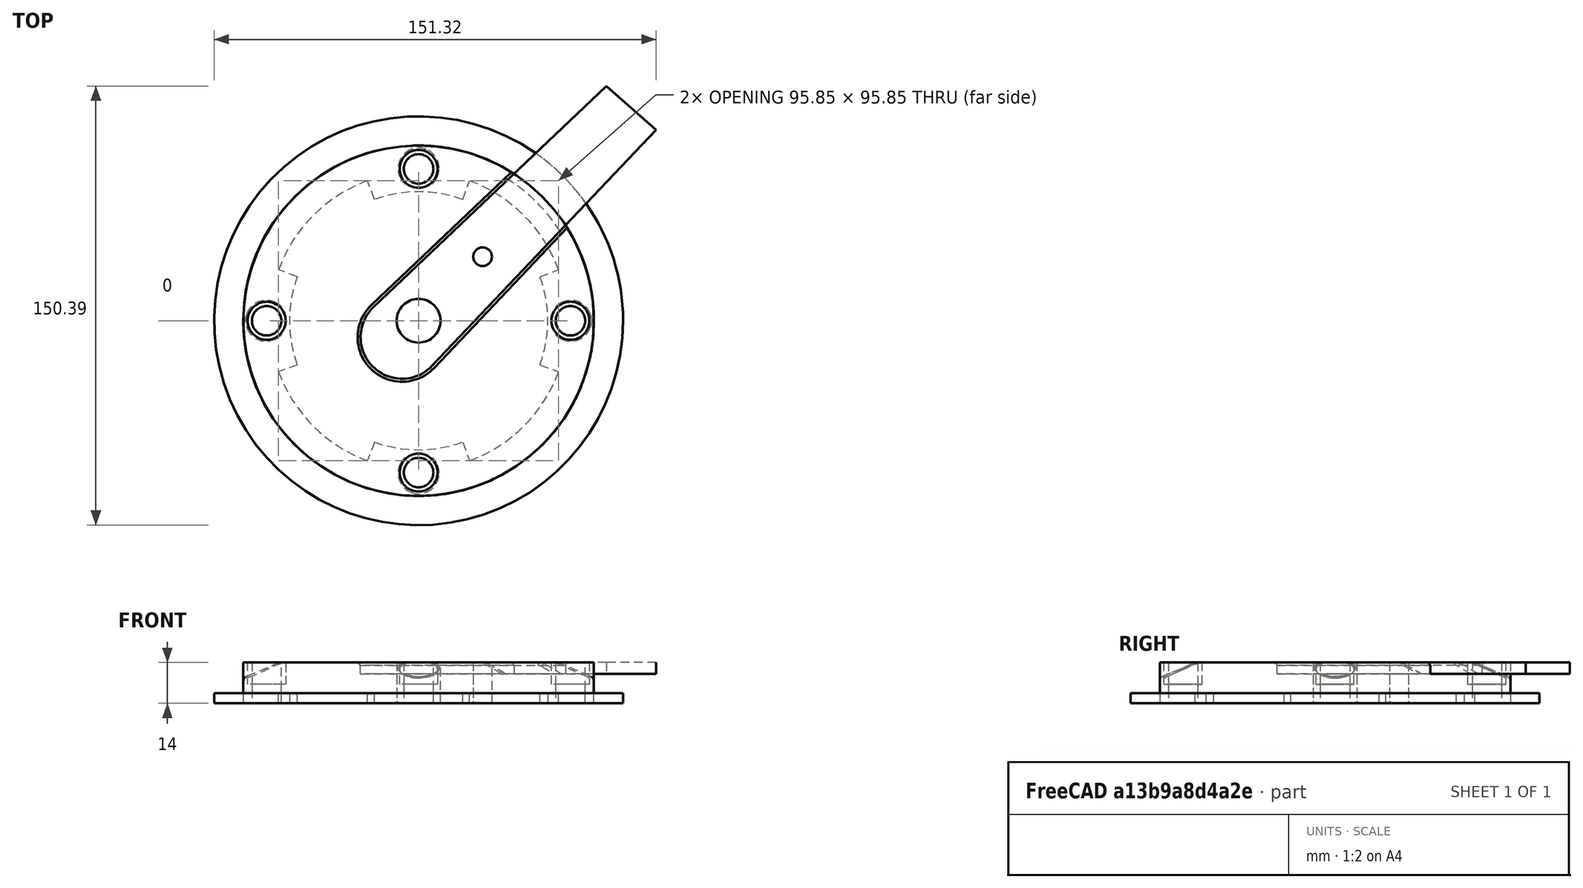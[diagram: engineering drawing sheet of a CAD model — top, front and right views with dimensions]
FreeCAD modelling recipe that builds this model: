
FCSTD DOCUMENT  (FreeCAD 0.16R)
Label: 104BCDspider_02
License: All rights reserved
LicenseURL: http://en.wikipedia.org/wiki/All_rights_reserved
objects: Sketcher::SketchObject×4, PartDesign::Fillet×4, PartDesign::Pocket×3, PartDesign::Pad×1, PartDesign::Chamfer×1, Part::Cone×1, Part::Common×1, Mesh::Feature×1
note: 19 computed .brp shape members not serialized (recipe doc carries the construction recipe); baked Part::Feature solids carry a one-line shape summary decoded from their .brp

FEATURE [Sketcher::SketchObject] Sketch
  sketch-geometry (9):
    g0: Circle [constr] CenterX=0 CenterY=0 CenterZ=0 NormalX=0 NormalY=0 NormalZ=1 Radius=52
    g1: Circle CenterX=0 CenterY=0 CenterZ=0 NormalX=0 NormalY=0 NormalZ=1 Radius=7.5
    g2: Circle CenterX=21.9203 CenterY=21.9203 CenterZ=0 NormalX=0 NormalY=0 NormalZ=1 Radius=3.2
    g3: Circle CenterX=0 CenterY=0 CenterZ=0 NormalX=0 NormalY=0 NormalZ=1 Radius=60
    g4: Circle CenterX=-52 CenterY=0 CenterZ=0 NormalX=0 NormalY=0 NormalZ=1 Radius=5.05
    g5: Circle CenterX=52 CenterY=0 CenterZ=0 NormalX=0 NormalY=0 NormalZ=1 Radius=5.05
    g6: Circle CenterX=0 CenterY=52 CenterZ=0 NormalX=0 NormalY=0 NormalZ=1 Radius=5.05
    g7: Circle CenterX=0 CenterY=-52 CenterZ=0 NormalX=0 NormalY=0 NormalZ=1 Radius=5.05
    g8: LineSegment [constr] StartX=0 StartY=0 StartZ=0 EndX=60.5216 EndY=60.5216 EndZ=0
  constraints (23):
    c: Coincident(g1,g-1)
    c: Coincident(g0,g-1)
    c: Radius(g0) = 52
    c: Radius(g1) = 7.5
    c: Radius(g2) = 3.2
    c: Coincident(g3,g-1)
    c: Radius(g3) = 60
    c: PointOnObject(g5,g-1)
    c: PointOnObject(g4,g-1)
    c: PointOnObject(g7,g-2)
    c: PointOnObject(g6,g-2)
    c: Radius(g7) = 5.05
    c: Equal(g7,g6)
    c: Equal(g7,g5)
    c: Equal(g7,g4)
    c: DistanceY(g7) = -52
    c: DistanceX(g5) = 52
    c: DistanceY(g6) = 52
    c: DistanceX(g4) = -52
    c: Distance(g-1,g2) = 31
    c: Coincident(g8,g-1)
    c: Angle(g8) = 0.785398
    c: PointOnObject(g2,g8)
FEATURE [PartDesign::Pad] Pad  label="Body14"
  Length = 14
  Length2 = 100
  Sketch = -> Sketch
  Type = 0
FEATURE [Sketcher::SketchObject] Sketch001
  Placement = pos=(0,0,0) rot=(1,0,0;3.14159rad)
  Support = -> Pad [Face8]
  sketch-geometry (17):
    g0: ArcOfCircle CenterX=0 CenterY=0 CenterZ=0 NormalX=0 NormalY=0 NormalZ=1 Radius=44.2 StartAngle=2.79253 EndAngle=3.49066
    g1: Circle CenterX=0 CenterY=0 CenterZ=0 NormalX=0 NormalY=0 NormalZ=1 Radius=70
    g2: ArcOfCircle CenterX=0 CenterY=0 CenterZ=0 NormalX=0 NormalY=0 NormalZ=1 Radius=51 StartAngle=1.91986 EndAngle=2.79253
    g3: LineSegment StartX=15.1173 StartY=41.5344 StartZ=0 EndX=17.443 EndY=47.9243 EndZ=0
    g4: LineSegment StartX=41.5344 StartY=15.1173 StartZ=0 EndX=47.9243 EndY=17.443 EndZ=0
    g5: LineSegment StartX=41.5344 StartY=-15.1173 StartZ=0 EndX=47.9243 EndY=-17.443 EndZ=0
    g6: LineSegment StartX=15.1173 StartY=-41.5344 StartZ=0 EndX=17.443 EndY=-47.9243 EndZ=0
    g7: LineSegment StartX=-15.1173 StartY=-41.5344 StartZ=0 EndX=-17.443 EndY=-47.9243 EndZ=0
    g8: LineSegment StartX=-41.5344 StartY=-15.1173 StartZ=0 EndX=-47.9243 EndY=-17.443 EndZ=0
    g9: LineSegment StartX=-41.5344 StartY=15.1173 StartZ=0 EndX=-47.9243 EndY=17.443 EndZ=0
    g10: LineSegment StartX=-15.1173 StartY=41.5344 StartZ=0 EndX=-17.443 EndY=47.9243 EndZ=0
    g11: ArcOfCircle CenterX=0 CenterY=0 CenterZ=0 NormalX=0 NormalY=0 NormalZ=1 Radius=51 StartAngle=0.349066 EndAngle=1.22173
    g12: ArcOfCircle CenterX=0 CenterY=0 CenterZ=0 NormalX=0 NormalY=0 NormalZ=1 Radius=51 StartAngle=5.06145 EndAngle=5.93412
    g13: ArcOfCircle CenterX=0 CenterY=0 CenterZ=0 NormalX=0 NormalY=0 NormalZ=1 Radius=51 StartAngle=3.49066 EndAngle=4.36332
    g14: ArcOfCircle CenterX=0 CenterY=0 CenterZ=0 NormalX=0 NormalY=0 NormalZ=1 Radius=44.2 StartAngle=1.22173 EndAngle=1.91986
    g15: ArcOfCircle CenterX=0 CenterY=0 CenterZ=0 NormalX=0 NormalY=0 NormalZ=1 Radius=44.2 StartAngle=5.93412 EndAngle=6.63225
    g16: ArcOfCircle CenterX=0 CenterY=0 CenterZ=0 NormalX=0 NormalY=0 NormalZ=1 Radius=44.2 StartAngle=4.36332 EndAngle=5.06145
  constraints (42):
    c: Coincident(g-1,g0)
    c: Radius(g0) = 44.2
    c: Coincident(g-1,g1)
    c: Radius(g1) = 70
    c: Coincident(g2,g-1)
    c: Radius(g2) = 51
    c: Angle(g3) = 1.22173
    c: Angle(g4) = 0.349066
    c: Angle(g5) = -0.349066
    c: Angle(g6) = -1.22173
    c: Angle(g7) = -1.91986
    c: Angle(g8) = -2.79253
    c: Angle(g9) = 2.79253
    c: Angle(g10) = 1.91986
    c: Equal(g2,g11)
    c: Coincident(g2,g11)
    c: Equal(g2,g12)
    c: Coincident(g2,g12)
    c: Equal(g2,g13)
    c: Coincident(g2,g13)
    c: Equal(g0,g14)
    c: Coincident(g0,g14)
    c: Equal(g0,g15)
    c: Coincident(g0,g15)
    c: Equal(g0,g16)
    c: Coincident(g0,g16)
    c: Coincident(g10,g14)
    c: Coincident(g3,g14)
    c: Coincident(g4,g15)
    c: Coincident(g5,g15)
    c: Coincident(g6,g16)
    c: Coincident(g9,g0)
    c: Coincident(g8,g0)
    c: Coincident(g7,g16)
    c: Coincident(g3,g11)
    c: Coincident(g10,g2)
    c: Coincident(g9,g2)
    c: Coincident(g8,g13)
    c: Coincident(g7,g13)
    c: Coincident(g6,g12)
    c: Coincident(g5,g12)
    c: Coincident(g4,g11)
FEATURE [PartDesign::Pocket] Pocket  label="Back3.5"
  Length = 3.5
  Sketch = -> Sketch001
  Type = 0
FEATURE [Sketcher::SketchObject] Sketch002
  ExternalGeometry = -> [Pocket]
  Placement = pos=(0,0,14) rot=(0,0,1;0rad)
  Support = -> Pocket [Face3]
  sketch-geometry (4):
    g0: LineSegment StartX=4.64454 StartY=-15.4397 StartZ=0 EndX=81.321 EndY=65.3005 EndZ=0
    g1: LineSegment StartX=81.321 StartY=65.3005 StartZ=0 EndX=64.3234 EndY=80.3931 EndZ=0
    g2: LineSegment StartX=64.3234 StartY=80.3931 StartZ=0 EndX=-15.4397 EndY=4.64454 EndZ=0
    g3: ArcOfCircle CenterX=-5.65685 CenterY=-5.65685 CenterZ=0 NormalX=0 NormalY=0 NormalZ=1 Radius=14.2065 StartAngle=2.33038 EndAngle=5.5236
  constraints (12):
    c: Coincident(g0,g1)
    c: Coincident(g1,g2)
    c: Distance(g2) = 110
    c: Distance(g-1,g0) = 14
    c: Distance(g-1,g2) = 14
    c: Tangent(g3,g2)
    c: Coincident(g3,g2)
    c: Coincident(g0,g3)
    c: Tangent(g3,g0)
    c: Distance(g-1,g3) = 8
    c: Distance(g-3,g0) = 13.2
    c: Distance(g-3,g2) = 13.2
FEATURE [PartDesign::Pocket] Pocket001  label="Front4"
  Length = 4
  Sketch = -> Sketch002
  Type = 0
FEATURE [Sketcher::SketchObject] Sketch003
  ExternalGeometry = -> [Pocket001]
  Placement = pos=(0,0,14) rot=(0,0,1;0rad)
  Support = -> Pocket001 [Face2]
  sketch-geometry (4):
    g0: Circle CenterX=0 CenterY=52 CenterZ=0 NormalX=0 NormalY=0 NormalZ=1 Radius=6.5
    g1: Circle CenterX=52 CenterY=0 CenterZ=0 NormalX=0 NormalY=0 NormalZ=1 Radius=6.5
    g2: Circle CenterX=0 CenterY=-52 CenterZ=0 NormalX=0 NormalY=0 NormalZ=1 Radius=6.5
    g3: Circle CenterX=-52 CenterY=0 CenterZ=0 NormalX=0 NormalY=0 NormalZ=1 Radius=6.5
  constraints (8):
    c: Coincident(g3,g-3)
    c: Coincident(g0,g-4)
    c: Coincident(g1,g-5)
    c: Coincident(g2,g-6)
    c: Radius(g0) = 6.5
    c: Equal(g0,g1)
    c: Equal(g0,g3)
    c: Equal(g0,g2)
FEATURE [PartDesign::Pocket] Pocket002
  Length = 7.5
  Sketch = -> Sketch003
  Type = 0
FEATURE [PartDesign::Chamfer] Chamfer
  Base = -> Pocket002 [Edge8]
  Size = 1
FEATURE [Part::Cone] Cone002
  Angle = 360
  Height = 22
  Radius1 = 80
  Radius2 = 30
FEATURE [Part::Common] Common
  Base = -> Pocket002
  Tool = -> Cone002
FEATURE [PartDesign::Fillet] Fillet
  Base = -> Common [Edge37,Edge25,Edge32,Edge29,Edge34]
  Radius = 5
FEATURE [PartDesign::Fillet] Fillet001
  Base = -> Fillet [Edge5]
  Radius = 2
FEATURE [PartDesign::Fillet] Fillet002
  Base = -> Fillet001 [Edge59]
  Radius = 1
FEATURE [PartDesign::Fillet] Fillet003
  Base = -> Fillet002 [Edge49,Edge60,Edge26,Edge45]
  Radius = 0.5
FEATURE [Mesh::Feature] Mesh  label="Fillet003 (Meshed)"
